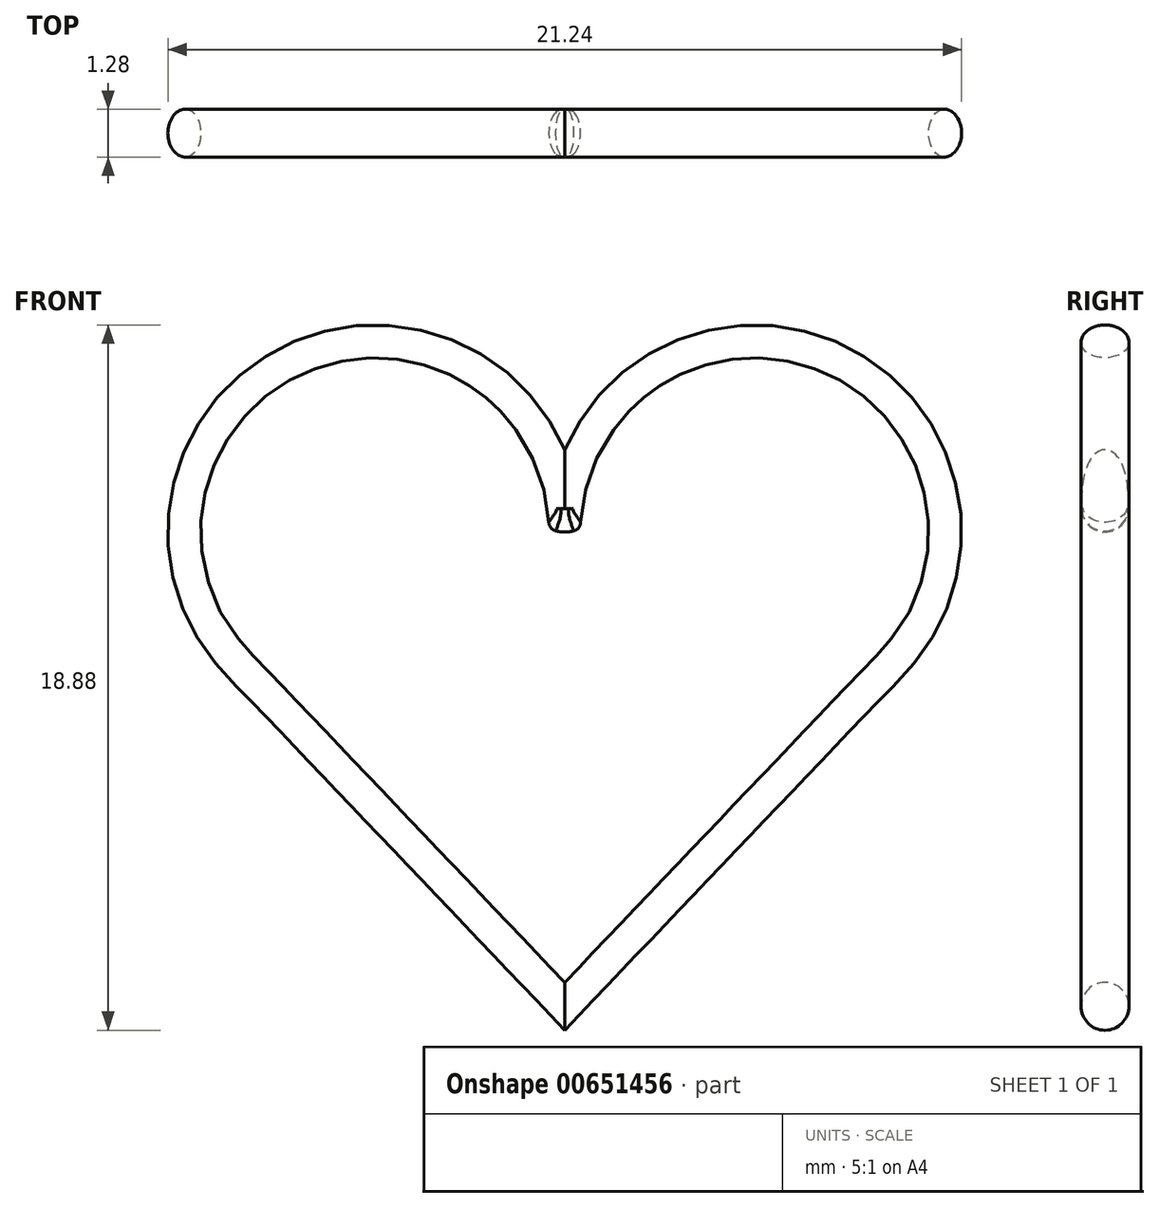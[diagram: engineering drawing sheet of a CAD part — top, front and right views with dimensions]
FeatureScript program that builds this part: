
annotation { "Feature Type Name" : "Feature", "Feature Type Description" : "" }
export const myFeature = defineFeature(function(context is Context, id is Id, definition is map)
    precondition{}
    {
        {
            var Q0;
            Q0=qCreatedBy(makeId("Front.planeOp"),FACE);
            var sketch = newSketch(context, id + "F0", { "sketchPlane" : qUnion([Q0])});
            skLineSegment(sketch, "E0", {"start": v(-8.76, 0) * mm, "end": v(0, -9.2) * mm});
            skArc(sketch, "E1", {"start": v(-8.76, 0) * mm, "mid": v(-6.97, 8.22) * mm, "end": v(0, 3.5) * mm});
            skLineSegment(sketch, "E2", {"start": v(0, 3.5) * mm, "end": v(0, -9.2) * mm, "construction": true});
            skArc(sketch, "E3.MirrorCS", {"start": v(8.76, 0) * mm, "mid": v(6.97, 8.22) * mm, "end": v(0, 3.5) * mm});
            skLineSegment(sketch, "E4.MirrorCS", {"start": v(8.76, 0) * mm, "end": v(0, -9.2) * mm});
            skSolve(sketch);
        }
        {
            var Q0;
            Q0=qCreatedBy(makeId("Right.planeOp"),FACE);
            var sketch = newSketch(context, id + "F1", { "sketchPlane" : qUnion([Q0])});
            skCircle(sketch, "E5", {"center": v(0, -9.2) * mm, "radius": 0.64 * mm});
            skSolve(sketch);
        }
        {
            var Q0;
            Q0 = qSketchRegion(id + "F1", true);
            var Q1;
            Q1=sQuery(id+"F0.wireOp",EDGE,"E0");
            var Q2;
            Q2=sQuery(id+"F0.wireOp",EDGE,"E1");
            sweep(context, id + "F2", {"profiles" : qUnion([Q0]), "path" : qUnion([Q1, Q2])});
        }
        {
            var Q0;
            Q0 = qSketchRegion(id + "F1", true);
            var Q1;
            Q1=sQuery(id+"F0.wireOp",EDGE,"E4.MirrorCS");
            var Q2;
            Q2=sQuery(id+"F0.wireOp",EDGE,"E3.MirrorCS");
            sweep(context, id + "F3", {"operationType" : NewBodyOperationType.ADD, "profiles" : qUnion([Q0]), "path" : qUnion([Q1, Q2])});
        }
        {
            var Q0;
            Q0=qCreatedBy(makeId("Front.planeOp"),FACE);
            var sketch = newSketch(context, id + "F4", { "sketchPlane" : qUnion([Q0])});
            skArc(sketch, "E6", {"start": v(0.94, 4.13) * mm, "mid": v(0, 3.5) * mm, "end": v(-0.94, 4.13) * mm});
            skLineSegment(sketch, "E7", {"start": v(-0.94, 4.13) * mm, "end": v(-1.26, 4.13) * mm});
            skLineSegment(sketch, "E8", {"start": v(-1.26, 4.13) * mm, "end": v(-1.26, 2.94) * mm});
            skLineSegment(sketch, "E9", {"start": v(-1.26, 2.94) * mm, "end": v(1.38, 2.94) * mm});
            skLineSegment(sketch, "E10", {"start": v(1.38, 2.94) * mm, "end": v(1.38, 4.13) * mm});
            skLineSegment(sketch, "E11", {"start": v(1.38, 4.13) * mm, "end": v(0.94, 4.13) * mm});
            skLineSegment(sketch, "E12", {"start": v(-0.94, 4.13) * mm, "end": v(0.94, 4.13) * mm, "construction": true});
            skSolve(sketch);
        }
        {
            var Q0;
            Q0 = qSketchRegion(id + "F4", true);
            var Q1;
            Q1 = qConstructionFilter(qBodyType(qCreatedBy(id + "F4" ,EDGE), BodyType.WIRE), ConstructionObject.NO);
            var Q2;
            Q2=sQuery(id+"F4.wireOp",EDGE,"E12");
            revolve(context, id + "F5", {"operationType" : NewBodyOperationType.REMOVE, "entities" : qUnion([Q0]), "surfaceEntities" : qUnion([Q1]), "axis" : qUnion([Q2]), "revolveType" : RevolveType.SYMMETRIC, "oppositeDirection" : true, "angle" : 180 * degree});
        }
        {
            var Q0;
            Q0=makeQuery(id+"F5.boolean.opBoolean","INTERSECT",EDGE,{"derivedFrom":[makeQuery(id+"F2.opSweep","SWEPT_FACE",FACE,{"disambiguationData":[OSD([sQuery(id+"F0.wireOp",EDGE,"E1"),sQuery(id+"F1.wireOp",EDGE,"E5")])]}),makeQuery(id+"F5.opRevolve","SWEPT_FACE",FACE,{"disambiguationData":[OSD([sQuery(id+"F4.wireOp",EDGE,"E6")])]})]});
            var Q1;
            Q1=makeQuery(id+"F5.boolean.opBoolean","INTERSECT",EDGE,{"derivedFrom":[makeQuery(id+"F3.opSweep","SWEPT_FACE",FACE,{"disambiguationData":[OSD([sQuery(id+"F0.wireOp",EDGE,"E3.MirrorCS"),sQuery(id+"F1.wireOp",EDGE,"E5")])]}),makeQuery(id+"F5.opRevolve","SWEPT_FACE",FACE,{"disambiguationData":[OSD([sQuery(id+"F4.wireOp",EDGE,"E6")])]})]});
            fillet(context, id + "F6", {"entities" : qUnion([Q0, Q1]), "radius" : 0.25 * mm, "tangentPropagation" : true, "allowEdgeOverflow" : false});
        }
    });
